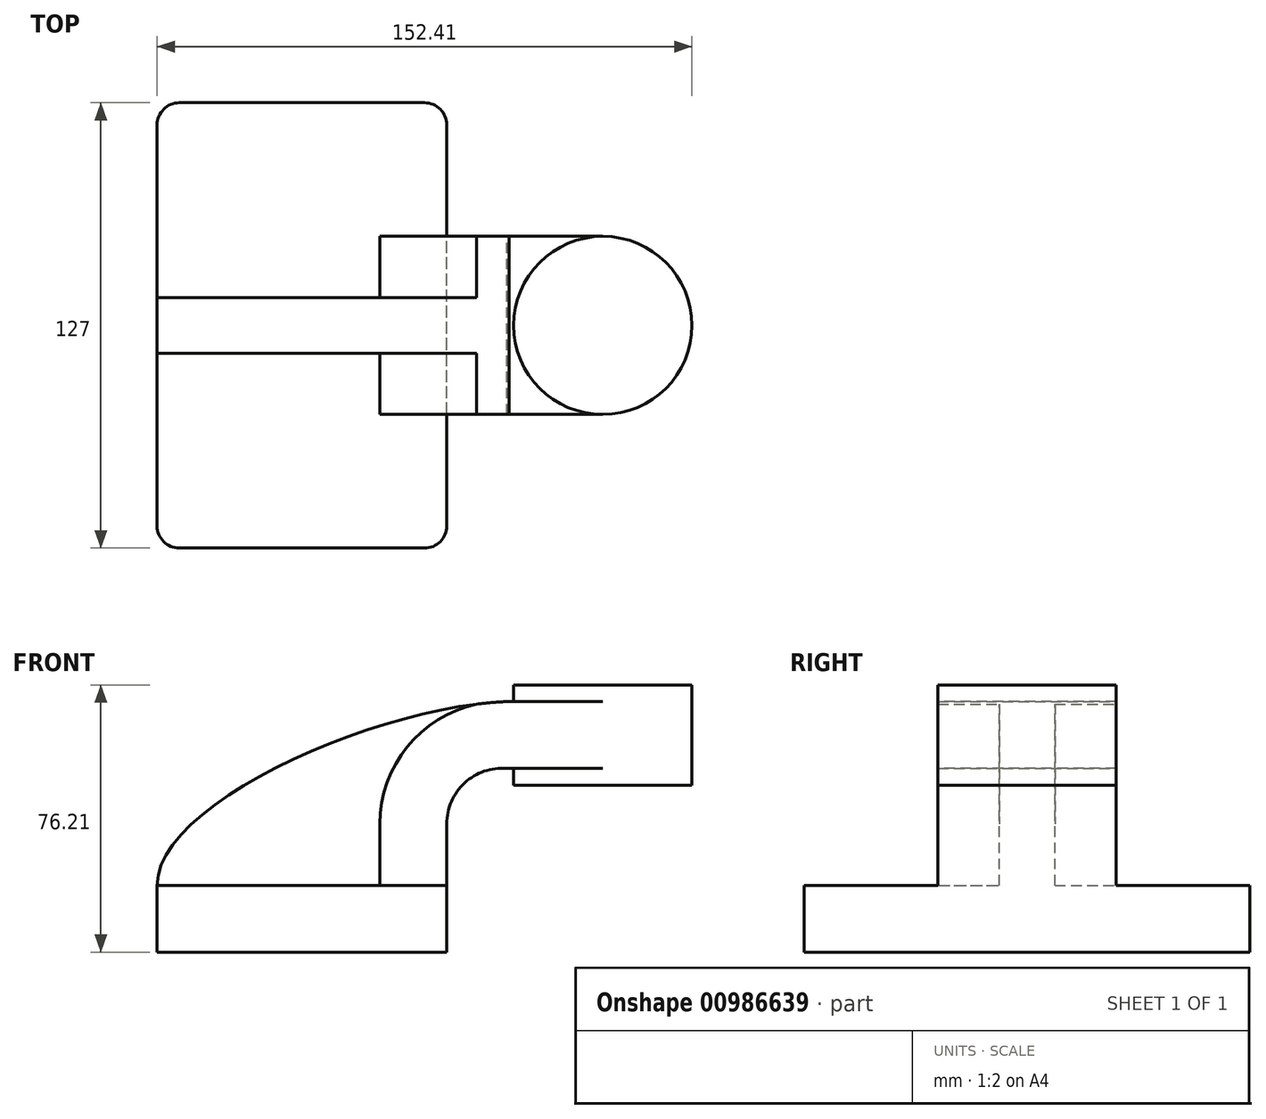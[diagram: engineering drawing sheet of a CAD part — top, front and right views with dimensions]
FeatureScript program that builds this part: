
annotation { "Feature Type Name" : "Feature", "Feature Type Description" : "" }
export const myFeature = defineFeature(function(context is Context, id is Id, definition is map)
    precondition{}
    {
        {
            var Q0;
            Q0=qCreatedBy(makeId("Front.planeOp"),FACE);
            var sketch = newSketch(context, id + "F0", { "sketchPlane" : qUnion([Q0])});
            skLineSegment(sketch, "E0.bottom", {"start": v(41.28, -9.52) * mm, "end": v(-41.28, -9.53) * mm});
            skLineSegment(sketch, "E0.top", {"start": v(41.27, 9.53) * mm, "end": v(-41.28, 9.53) * mm});
            skLineSegment(sketch, "E0.left", {"start": v(41.28, -9.52) * mm, "end": v(41.28, 9.53) * mm});
            skLineSegment(sketch, "E0.right", {"start": v(-41.27, -9.53) * mm, "end": v(-41.28, 9.53) * mm});
            skPoint(sketch, "E0.middle", {"position": v(0, 0) * mm});
            skLineSegment(sketch, "E1.bottom", {"start": v(60.32, 38.1) * mm, "end": v(111.12, 38.1) * mm});
            skLineSegment(sketch, "E1.top", {"start": v(60.32, 66.68) * mm, "end": v(111.12, 66.68) * mm});
            skLineSegment(sketch, "E1.left", {"start": v(60.32, 38.1) * mm, "end": v(60.32, 66.68) * mm});
            skLineSegment(sketch, "E1.right", {"start": v(111.12, 38.1) * mm, "end": v(111.12, 66.68) * mm});
            skPoint(sketch, "E1.middle", {"position": v(85.72, 52.39) * mm});
            skLineSegment(sketch, "E2", {"start": v(41.27, 9.53) * mm, "end": v(41.27, 27.05) * mm});
            skArc(sketch, "E3", {"start": v(41.27, 27.05) * mm, "mid": v(46.37, 38.7) * mm, "end": v(58.4, 42.88) * mm});
            skLineSegment(sketch, "E4", {"start": v(58.4, 42.88) * mm, "end": v(85.73, 42.88) * mm});
            skLineSegment(sketch, "E5.0", {"start": v(59, 61.93) * mm, "end": v(85.72, 61.93) * mm});
            skArc(sketch, "E5.1", {"start": v(22.22, 27.05) * mm, "mid": v(33.11, 52.39) * mm, "end": v(59, 61.93) * mm});
            skLineSegment(sketch, "E5.2", {"start": v(22.22, 9.53) * mm, "end": v(22.22, 27.05) * mm});
            skPoint(sketch, "E6.endSnap0", {"position": v(85.72, 66.68) * mm});
            skFitSpline(sketch, "E7", {"points": [v(-41.28, 9.52) * mm, v(59, 61.93) * mm], "startDerivative": vector(-0.26, 70.6) * mm, "endDerivative": vector(111.76, 3.26) * mm});
            skPoint(sketch, "E8.endSnap0", {"position": v(85.72, 38.1) * mm});
            skLineSegment(sketch, "E9", {"start": v(85.72, 66.68) * mm, "end": v(85.72, 38.1) * mm});
            skSolve(sketch);
        }
        {
            var Q0;
            Q0=makeQuery(id+"F0.imprint","IMPRINT",FACE,{"disambiguationData":[TD([[makeQuery(id+"F0.imprint","IMPRINT",EDGE,{"derivedFrom":sQuery(id+"F0.wireOp",EDGE,"E0.bottom")}),-1.0]])]});
            extrude(context, id + "F1", {"entities" : qUnion([Q0]), "endBound" : BoundingType.SYMMETRIC, "depth" : 127 * mm, "offsetDistance" : 25.4 * mm});
        }
        {
            var Q0;
            {var subQ1=sQuery(id+"F0.wireOp",EDGE,"E2");Q0=makeQuery(id+"F0.imprint","IMPRINT",FACE,{"disambiguationData":[TD([[makeQuery(id+"F0.imprint","IMPRINT",EDGE,{"derivedFrom":subQ1}),1.0]])]});}
            var Q1;
            {var subQ0=sQuery(id+"F0.wireOp",EDGE,"E4");var subQ1=sQuery(id+"F0.wireOp",EDGE,"E1.left");var subQ2=makeQuery(id+"F0.imprint","INTERSECT",VERTEX,{"derivedFrom":[subQ1,subQ0]});Q1=makeQuery(id+"F0.imprint","IMPRINT",FACE,{"disambiguationData":[TD([[makeQuery(id+"F0.imprint","IMPRINT",EDGE,{"disambiguationData":[TD([[subQ2,-1.0]])],"derivedFrom":subQ1}),-1.0]])]});}
            extrude(context, id + "F2", {"entities" : qUnion([Q0, Q1]), "operationType" : NewBodyOperationType.ADD, "endBound" : BoundingType.SYMMETRIC, "depth" : 50.8 * mm, "offsetDistance" : 25.4 * mm});
        }
        {
            var Q0;
            {var subQ3=sQuery(id+"F0.wireOp",EDGE,"E5.2");Q0=makeQuery(id+"F0.imprint","IMPRINT",FACE,{"disambiguationData":[TD([[makeQuery(id+"F0.imprint","IMPRINT",EDGE,{"derivedFrom":subQ3}),1.0]])]});}
            extrude(context, id + "F3", {"entities" : qUnion([Q0]), "operationType" : NewBodyOperationType.ADD, "endBound" : BoundingType.SYMMETRIC, "depth" : 15.88 * mm, "offsetDistance" : 25.4 * mm});
        }
        {
            var Q0;
            {var subQ4=sQuery(id+"F0.wireOp",EDGE,"E1.right");Q0=makeQuery(id+"F0.imprint","IMPRINT",FACE,{"disambiguationData":[TD([[makeQuery(id+"F0.imprint","IMPRINT",EDGE,{"derivedFrom":subQ4}),1.0]])]});}
            var Q1;
            Q1=sQuery(id+"F0.wireOp",EDGE,"E9");
            revolve(context, id + "F4", {"operationType" : NewBodyOperationType.ADD, "surfaceOperationType" : NewSurfaceOperationType.NEW, "entities" : qUnion([Q0]), "axis" : qUnion([Q1]), "revolveType" : RevolveType.FULL});
        }
        {
            var Q0;
            Q0=makeQuery(id+"F1.opExtrude","CAP_EDGE",EDGE,{"disambiguationData":[OSD([sQuery(id+"F0.wireOp",EDGE,"E0.right")])],"isStart":false});
            var Q1;
            Q1=makeQuery(id+"F1.opExtrude","CAP_EDGE",EDGE,{"disambiguationData":[OSD([sQuery(id+"F0.wireOp",EDGE,"E0.left")])],"isStart":false});
            var Q2;
            Q2=makeQuery(id+"F1.opExtrude","CAP_EDGE",EDGE,{"disambiguationData":[OSD([sQuery(id+"F0.wireOp",EDGE,"E0.left")])],"isStart":true});
            var Q3;
            Q3=makeQuery(id+"F1.opExtrude","CAP_EDGE",EDGE,{"disambiguationData":[OSD([sQuery(id+"F0.wireOp",EDGE,"E0.right")])],"isStart":true});
            fillet(context, id + "F5", {"entities" : qUnion([Q0, Q1, Q2, Q3]), "radius" : 6.35 * mm, "tangentPropagation" : true, "allowEdgeOverflow" : false});
        }
    });
